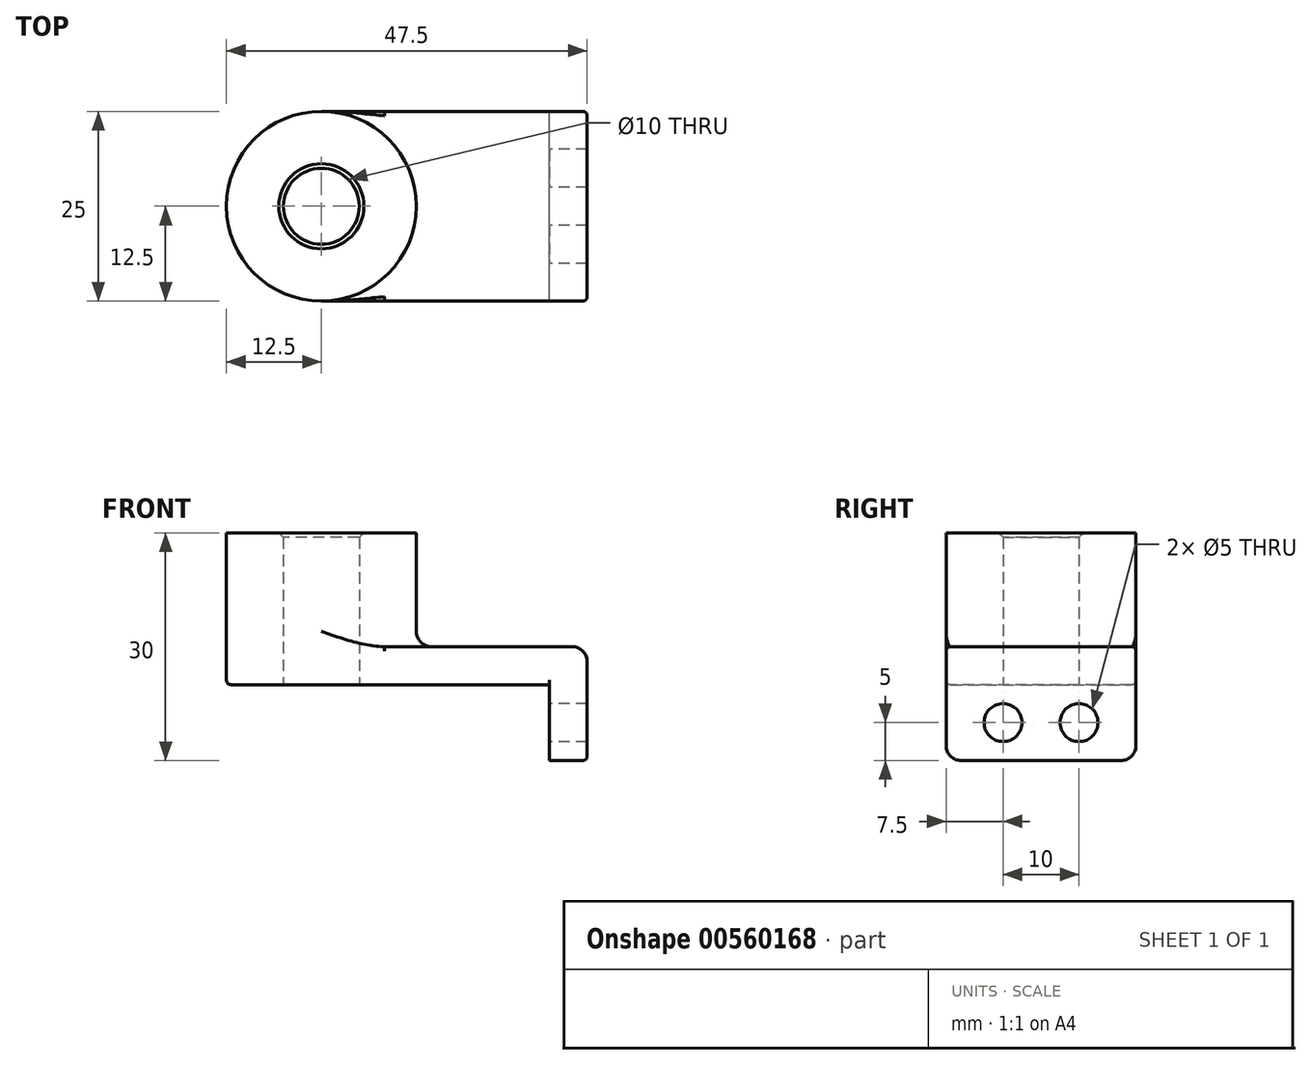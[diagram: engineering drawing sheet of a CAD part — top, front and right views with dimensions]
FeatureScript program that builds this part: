
annotation { "Feature Type Name" : "Feature", "Feature Type Description" : "" }
export const myFeature = defineFeature(function(context is Context, id is Id, definition is map)
    precondition{}
    {
        {
            var Q0;
            Q0=qCreatedBy(makeId("Top.planeOp"),FACE);
            var sketch = newSketch(context, id + "F0", { "sketchPlane" : qUnion([Q0])});
            skLineSegment(sketch, "E0.bottom", {"start": v(15, -12.5) * mm, "end": v(-15, -12.5) * mm});
            skLineSegment(sketch, "E0.top", {"start": v(15, 12.5) * mm, "end": v(-15, 12.5) * mm});
            skLineSegment(sketch, "E0.left", {"start": v(15, -12.5) * mm, "end": v(15, 12.5) * mm});
            skLineSegment(sketch, "E0.right", {"start": v(-15, -12.5) * mm, "end": v(-15, 12.5) * mm});
            skPoint(sketch, "E0.middle", {"position": v(0, 0) * mm});
            skCircle(sketch, "E1", {"center": v(-15, 0) * mm, "radius": 12.5 * mm});
            skCircle(sketch, "E2", {"center": v(-15, 0) * mm, "radius": 5 * mm});
            skSolve(sketch);
        }
        {
            var Q0;
            Q0 = qSketchRegion(id + "F0", true);
            extrude(context, id + "F1", {"entities" : qUnion([Q0]), "depth" : 5 * mm, "offsetDistance" : 25 * mm});
        }
        {
            var Q0;
            {var subQ1=sQuery(id+"F0.wireOp",EDGE,"E0.right");var subQ3=sQuery(id+"F0.wireOp",EDGE,"E2");var subQ4=makeQuery(id+"F0.imprint","INTERSECT",VERTEX,{"disambiguationData":[OD(0.0)],"derivedFrom":[subQ1,subQ3]});Q0=makeQuery(id+"F0.imprint","IMPRINT",FACE,{"disambiguationData":[TD([[makeQuery(id+"F0.imprint","IMPRINT",EDGE,{"disambiguationData":[TD([[subQ4,1.0]])],"derivedFrom":subQ3}),-1.0]])]});}
            var Q1;
            {var subQ1=sQuery(id+"F0.wireOp",EDGE,"E0.right");var subQ3=sQuery(id+"F0.wireOp",EDGE,"E2");var subQ4=makeQuery(id+"F0.imprint","INTERSECT",VERTEX,{"disambiguationData":[OD(0.0)],"derivedFrom":[subQ1,subQ3]});Q1=makeQuery(id+"F0.imprint","IMPRINT",FACE,{"disambiguationData":[TD([[makeQuery(id+"F0.imprint","IMPRINT",EDGE,{"disambiguationData":[TD([[subQ4,-1.0]])],"derivedFrom":subQ3}),-1.0]])]});}
            extrude(context, id + "F2", {"entities" : qUnion([Q0, Q1]), "operationType" : NewBodyOperationType.ADD, "depth" : 20 * mm, "offsetDistance" : 25 * mm});
        }
        {
            var Q0;
            Q0=makeQuery(id+"F1.opExtrude","SWEPT_FACE",FACE,{"disambiguationData":[OSD([sQuery(id+"F0.wireOp",EDGE,"E0.left")])]});
            var sketch = newSketch(context, id + "F3", { "sketchPlane" : qUnion([Q0])});
            skLineSegment(sketch, "E3.bottom", {"start": v(-12.5, 5) * mm, "end": v(12.5, 5) * mm});
            skLineSegment(sketch, "E3.top", {"start": v(-12.5, -10) * mm, "end": v(12.5, -10) * mm});
            skLineSegment(sketch, "E3.left", {"start": v(-12.5, 5) * mm, "end": v(-12.5, -10) * mm});
            skLineSegment(sketch, "E3.right", {"start": v(12.5, 5) * mm, "end": v(12.5, -10) * mm});
            skCircle(sketch, "E4", {"center": v(-5, -5) * mm, "radius": 2.5 * mm});
            skLineSegment(sketch, "E5", {"start": v(0, 0) * mm, "end": v(0, -10) * mm});
            skCircle(sketch, "E6.MirrorC", {"center": v(5, -5) * mm, "radius": 2.5 * mm});
            skSolve(sketch);
        }
        {
            var Q0;
            Q0 = qSketchRegion(id + "F3", true);
            extrude(context, id + "F4", {"entities" : qUnion([Q0]), "operationType" : NewBodyOperationType.ADD, "depth" : 5 * mm, "offsetDistance" : 25 * mm});
        }
        {
            var Q0;
            {var subQ0=sQuery(id+"F0.wireOp",EDGE,"E1");Q0=makeQuery(id+"F2.boolean.opBoolean","INTERSECT",EDGE,{"derivedFrom":[makeQuery(id+"F1.opExtrude","CAP_FACE",FACE,{"disambiguationData":[OSD([sQuery(id+"F0.wireOp",EDGE,"E0.bottom"),sQuery(id+"F0.wireOp",EDGE,"E0.top"),sQuery(id+"F0.wireOp",EDGE,"E0.left"),subQ0,sQuery(id+"F0.wireOp",EDGE,"E2")])],"isStart":false}),makeQuery(id+"F2.opExtrude","SWEPT_FACE",FACE,{"disambiguationData":[OSD([subQ0])]})]});}
            var Q1;
            Q1=makeQuery(id+"F4.opExtrude","CAP_EDGE",EDGE,{"disambiguationData":[OSD([sQuery(id+"F3.wireOp",EDGE,"E3.bottom")])],"isStart":false});
            var Q2;
            Q2=makeQuery(id+"F4.opExtrude","SWEPT_EDGE",EDGE,{"disambiguationData":[OSD([sQuery(id+"F3.wireOp",EDGE,"E3.top"),sQuery(id+"F3.wireOp",EDGE,"E3.left")])]});
            var Q3;
            Q3=makeQuery(id+"F4.opExtrude","SWEPT_EDGE",EDGE,{"disambiguationData":[OSD([sQuery(id+"F3.wireOp",EDGE,"E3.top"),sQuery(id+"F3.wireOp",EDGE,"E3.right")])]});
            fillet(context, id + "F5", {"entities" : qUnion([Q0, Q1, Q2, Q3]), "radius" : 2 * mm, "tangentPropagation" : true, "allowEdgeOverflow" : false});
        }
        {
            var Q0;
            Q0=makeQuery(id+"F4.boolean.opBoolean","MERGE",EDGE,{"derivedFrom":[makeQuery(id+"F1.opExtrude","CAP_EDGE",EDGE,{"disambiguationData":[OSD([sQuery(id+"F0.wireOp",EDGE,"E0.bottom")])],"isStart":false}),makeQuery(id+"F4.opExtrude","SWEPT_EDGE",EDGE,{"disambiguationData":[OSD([sQuery(id+"F3.wireOp",EDGE,"E3.bottom"),sQuery(id+"F3.wireOp",EDGE,"E3.left")])]})]});
            var Q1;
            Q1=makeQuery(id+"F1.opExtrude","CAP_EDGE",EDGE,{"disambiguationData":[OSD([sQuery(id+"F0.wireOp",EDGE,"E0.bottom")])],"isStart":true});
            var Q2;
            Q2=makeQuery(id+"F1.opExtrude","CAP_EDGE",EDGE,{"disambiguationData":[OSD([sQuery(id+"F0.wireOp",EDGE,"E0.left")])],"isStart":true});
            fillet(context, id + "F6", {"entities" : qUnion([Q0, Q1, Q2]), "radius" : 0.6 * mm, "tangentPropagation" : true, "allowEdgeOverflow" : false});
        }
        {
            var Q0;
            Q0=makeQuery(id+"F2.opExtrude","CAP_EDGE",EDGE,{"disambiguationData":[OSD([sQuery(id+"F0.wireOp",EDGE,"E2")])],"isStart":false});
            chamfer(context, id + "F7", {"entities" : qUnion([Q0]), "width" : 0.6 * mm, "tangentPropagation" : true});
        }
    });
